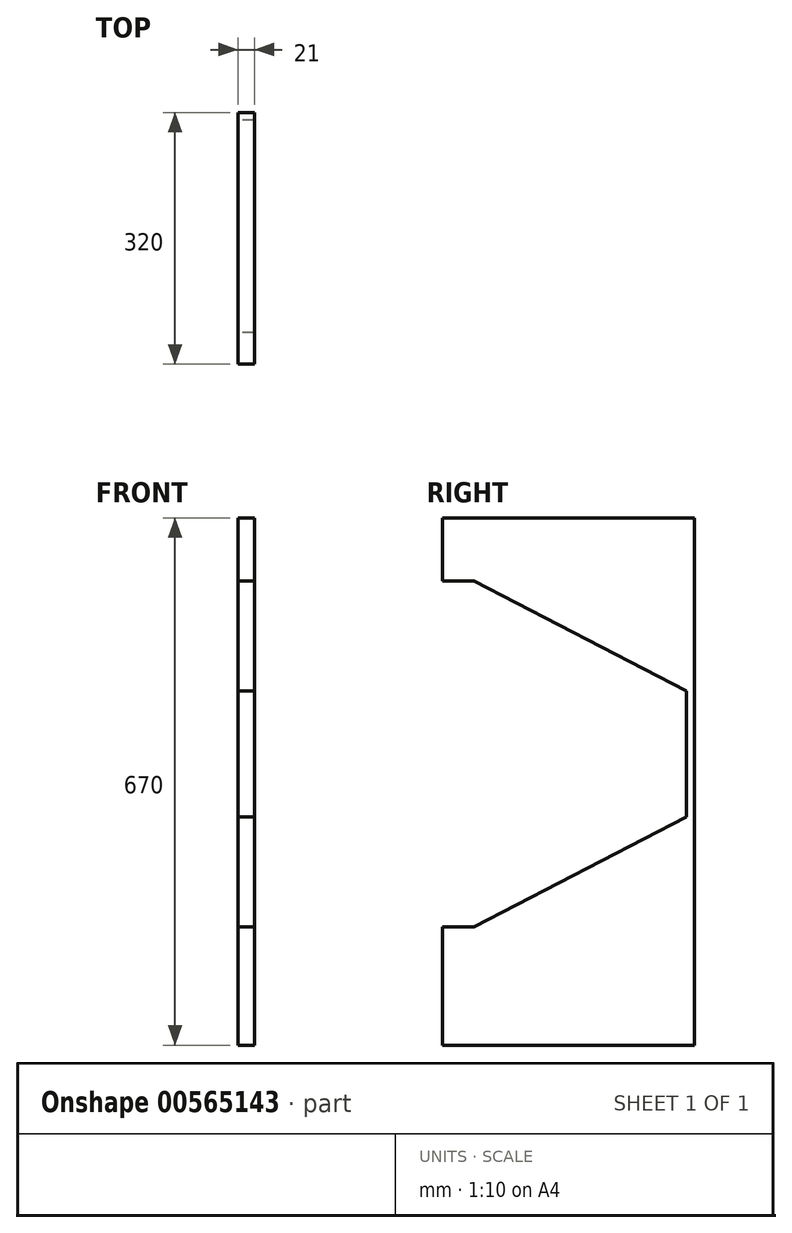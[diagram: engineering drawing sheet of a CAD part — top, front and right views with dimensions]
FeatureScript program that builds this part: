
annotation { "Feature Type Name" : "Feature", "Feature Type Description" : "" }
export const myFeature = defineFeature(function(context is Context, id is Id, definition is map)
    precondition{}
    {
        {
            var Q0;
            Q0=qCreatedBy(makeId("Right.planeOp"),FACE);
            var sketch = newSketch(context, id + "F0", { "sketchPlane" : qUnion([Q0])});
            skLineSegment(sketch, "E0.bottom", {"start": v(160, 335) * mm, "end": v(-160, 335) * mm});
            skLineSegment(sketch, "E0.top", {"start": v(160, -335) * mm, "end": v(-160, -335) * mm});
            skLineSegment(sketch, "E0.left", {"start": v(160, 335) * mm, "end": v(160, -335) * mm});
            skLineSegment(sketch, "E0.right", {"start": v(-160, 335) * mm, "end": v(-160, -335) * mm});
            skPoint(sketch, "E0.middle", {"position": v(0, 0) * mm});
            skPoint(sketch, "E1", {"position": v(-160, 255) * mm});
            skPoint(sketch, "E2", {"position": v(-160, -185) * mm});
            skPoint(sketch, "E3", {"position": v(160, 35) * mm});
            skPoint(sketch, "E4", {"position": v(80, 35) * mm});
            skPoint(sketch, "E5", {"position": v(160, 115) * mm});
            skPoint(sketch, "E6", {"position": v(160, -45) * mm});
            skPoint(sketch, "E7", {"position": v(-120, -185) * mm});
            skPoint(sketch, "E8", {"position": v(-120, 255) * mm});
            skLineSegment(sketch, "E9", {"start": v(-160, -185) * mm, "end": v(-120, -185) * mm});
            skPoint(sketch, "E10", {"position": v(150, -45) * mm});
            skPoint(sketch, "E11", {"position": v(150, 115) * mm});
            skLineSegment(sketch, "E12", {"start": v(-120, -185) * mm, "end": v(150, -45) * mm});
            skLineSegment(sketch, "E13", {"start": v(150, -45) * mm, "end": v(150, 115) * mm});
            skLineSegment(sketch, "E14", {"start": v(150, 115) * mm, "end": v(-120, 255) * mm});
            skLineSegment(sketch, "E15", {"start": v(-120, 255) * mm, "end": v(-160, 255) * mm});
            skSolve(sketch);
        }
        {
            var Q0;
            {var subQ1=sQuery(id+"F0.wireOp",EDGE,"E0.bottom");Q0=makeQuery(id+"F0.imprint","IMPRINT",FACE,{"disambiguationData":[TD([[makeQuery(id+"F0.imprint","IMPRINT",EDGE,{"derivedFrom":subQ1}),1.0]])]});}
            extrude(context, id + "F1", {"entities" : qUnion([Q0]), "depth" : 21 * mm, "offsetDistance" : 25 * mm});
        }
    });
